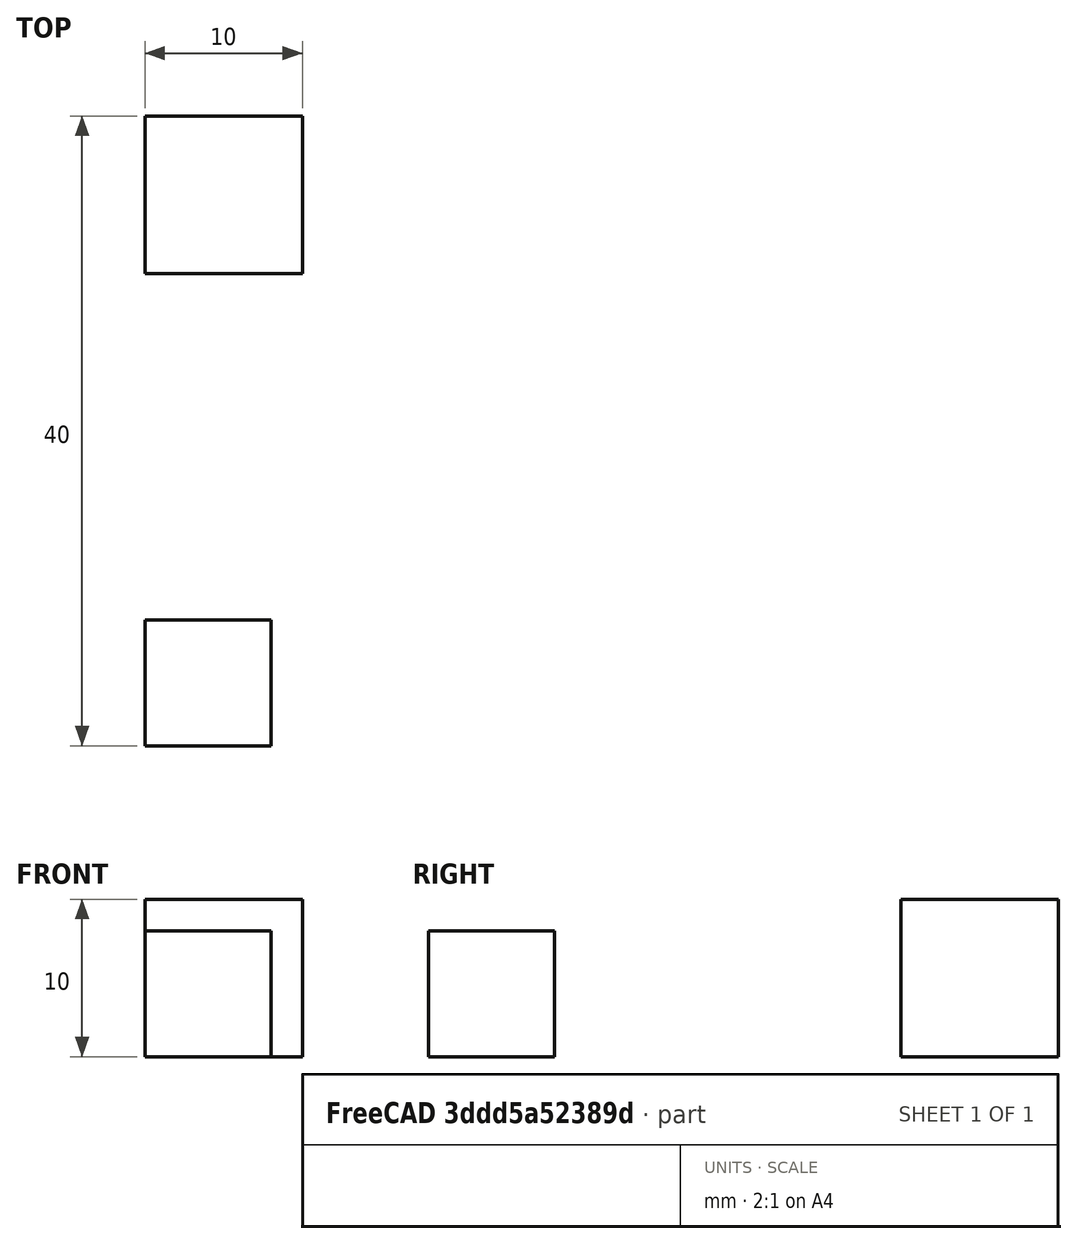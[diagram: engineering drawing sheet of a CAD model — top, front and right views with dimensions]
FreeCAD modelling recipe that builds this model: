
FCSTD DOCUMENT  (FreeCAD 0.16R6706 (Git))
Label: 80pc_rule
License: All rights reserved
LicenseURL: http://en.wikipedia.org/wiki/All_rights_reserved
objects: Part::Box×2, Part::MultiFuse×1, Drawing::FeatureViewPart×1, Drawing::FeaturePage×1
note: 3 computed .brp shape members not serialized (recipe doc carries the construction recipe); baked Part::Feature solids carry a one-line shape summary decoded from their .brp

FEATURE [Part::Box] Box  label="Cube"
  Height = 10
  Length = 10
  Width = 10
FEATURE [Part::Box] Box008  label="Cube008"
  Height = 8
  Length = 8
  Placement = pos=(0,-30,0) rot=(0,0,1;0rad)
  Width = 8
FEATURE [Part::MultiFuse] Fusion
  Shapes = -> [Box,Box008]
FEATURE [Drawing::FeatureViewPart] View
  Direction = (1,-1,1)
  HiddenWidth = 0.15
  LineWidth = 0.35
  Rotation = 60
  ShowHiddenLines = false
  ShowSmoothLines = false
  Source = -> Fusion
  Tolerance = 0.05
  ViewResult = <g id="View"\n   transform="rotate(60,108.536,146.867) translate(108.536,146.867) scale(1,1)"\n  >\n<g   stroke="rgb(0, 0, 0)"\n   stroke-width="0.35"\n   stroke-linecap="butt"\n   stroke-linejoin="miter"\n   fill="none"\n   transform="scale(1,-1)"\n  >\n<path id= "1" d=" M 0 0 L -7.07107 4.08248 " />\n<path id= "2" d=" M -7.07107 4.08248 L -7.07107 12.2474 " />\n<path id= "3" d=" M 7.07107 4.08248 L -8.88178e-16 8.16497 " />\n<path id= "4" d=" M 0 8.16497 L 0 16.3299 " />\n<path id= "5" d=" M 7.07107 12.2474 L -8.88178e-16 16.3299 " />\n<path id= "6" d=" M 7.07107 4.08248 L 7.07107 12.2474 " />\n<path id= "7" d=" M 0 0 L 7.07107 4.08248 " />\n<path id= "8" d=" M -7.07107 4.08248 L 8.88178e-16 8.16497 " />\n<path id= "9" d=" M -7.07107 12.2474 L 8.88178e-16 16.3299 " />\n<path id= "10" d=" M 0 -24.4949 L -5.65685 -21.2289 " />\n<path id= "11" d=" M -5.65685 -21.2289 L -5.65685 -14.6969 " />\n<path id= "12" d=" M 5.65685 -21.2289 L -8.88178e-16 -17.9629 " />\n<path id= "13" d=" M 0 -17.9629 L 0 -11.431 " />\n<path id= "14" d=" M 5.65685 -14.6969 L -8.88178e-16 -11.431 " />\n<path id= "15" d=" M 5.65685 -21.2289 L 5.65685 -14.6969 " />\n<path id= "16" d=" M 0 -24.4949 L 5.65685 -21.2289 " />\n<path id= "17" d=" M -5.65685 -21.2289 L 8.88178e-16 -17.9629 " />\n<path id= "18" d=" M -5.65685 -14.6969 L 8.88178e-16 -11.431 " />\n</g>\n</g>
  Visible = true
  X = 108.536
  Y = 146.867
FEATURE [Drawing::FeaturePage] Page
  Group = -> [View]
